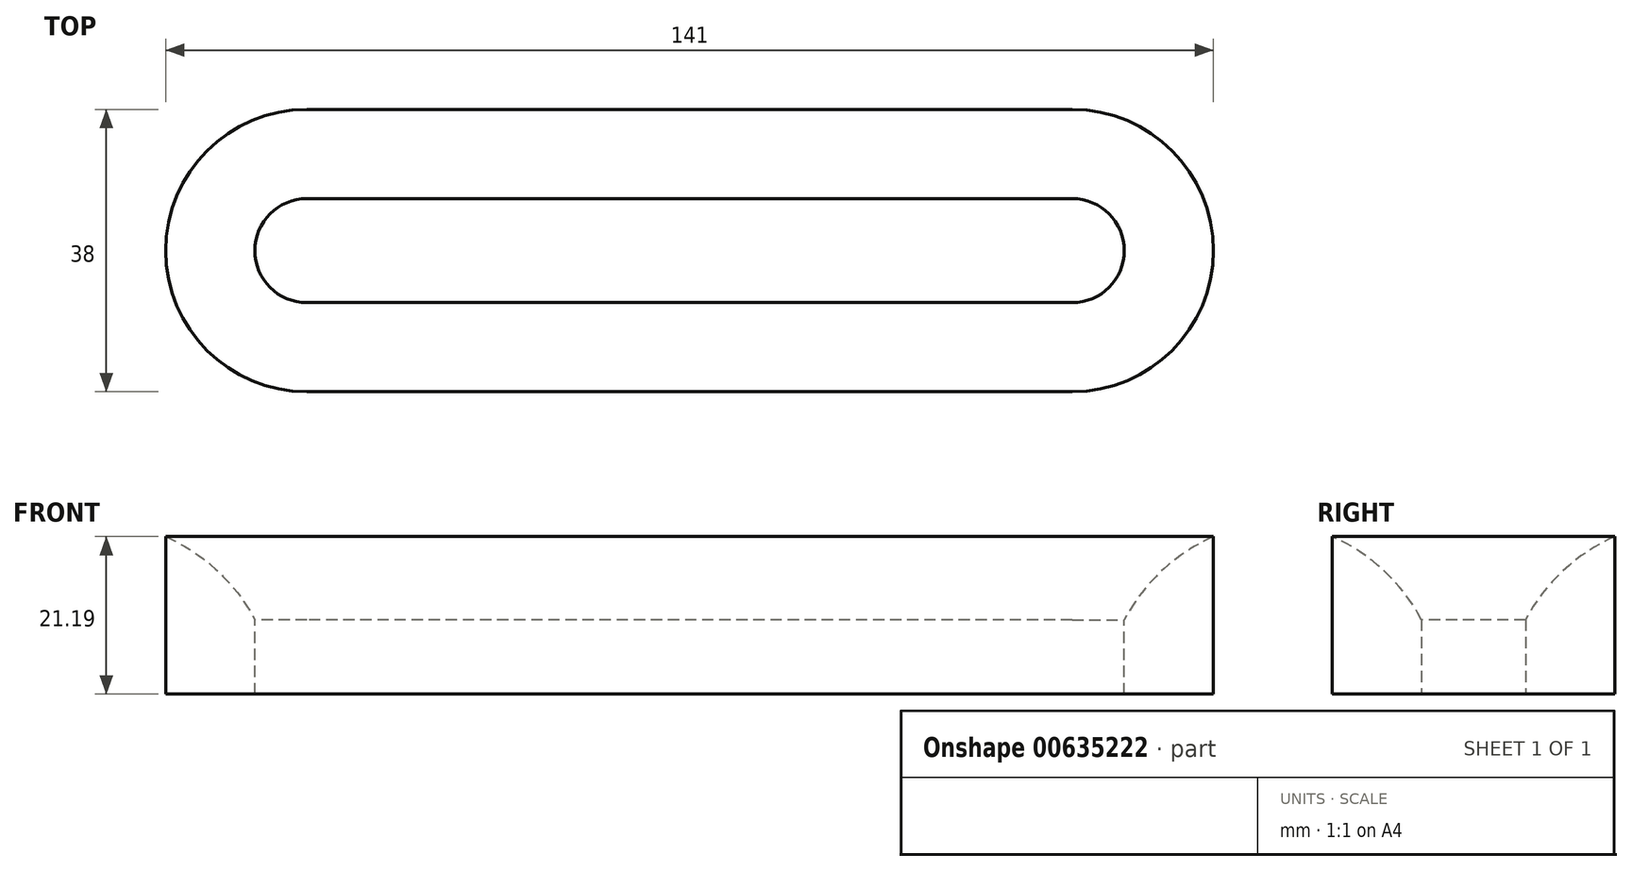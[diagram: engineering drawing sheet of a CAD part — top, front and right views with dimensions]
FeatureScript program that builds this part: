
annotation { "Feature Type Name" : "Feature", "Feature Type Description" : "" }
export const myFeature = defineFeature(function(context is Context, id is Id, definition is map)
    precondition{}
    {
        {
            var Q0;
            Q0=qCreatedBy(makeId("Top.planeOp"),FACE);
            var sketch = newSketch(context, id + "F0", { "sketchPlane" : qUnion([Q0])});
            skLineSegment(sketch, "E0", {"start": v(-51.5, 19) * mm, "end": v(51.5, 19) * mm});
            skLineSegment(sketch, "E1", {"start": v(-51.5, -19) * mm, "end": v(51.5, -19) * mm});
            skArc(sketch, "E2", {"start": v(-51.5, 19) * mm, "mid": v(-70.5, 0) * mm, "end": v(-51.5, -19) * mm});
            skArc(sketch, "E3", {"start": v(51.5, -19) * mm, "mid": v(70.5, 0) * mm, "end": v(51.5, 19) * mm});
            skSolve(sketch);
        }
        {
            var Q0;
            Q0=qCreatedBy(makeId("Right.planeOp"),FACE);
            var sketch = newSketch(context, id + "F1", { "sketchPlane" : qUnion([Q0])});
            skArc(sketch, "E4", {"start": v(-7, -11.2) * mm, "mid": v(-12.06, -4.58) * mm, "end": v(-19, 0) * mm});
            skLineSegment(sketch, "E5", {"start": v(-19, 0) * mm, "end": v(-19, -11.2) * mm});
            skLineSegment(sketch, "E6", {"start": v(-7, -11.2) * mm, "end": v(-7, -21.2) * mm});
            skLineSegment(sketch, "E7", {"start": v(-7, -21.2) * mm, "end": v(-19, -21.2) * mm});
            skLineSegment(sketch, "E8", {"start": v(-19, -21.2) * mm, "end": v(-19, -11.2) * mm});
            skSolve(sketch);
        }
        {
            var Q0;
            Q0=makeQuery(id+"F1.imprint","IMPRINT",FACE,{"disambiguationData":[TD([[makeQuery(id+"F1.imprint","IMPRINT",EDGE,{"derivedFrom":sQuery(id+"F1.wireOp",EDGE,"E4")}),1.0]])]});
            var Q1;
            Q1=sQuery(id+"F0.wireOp",EDGE,"E1");
            var Q2;
            Q2=sQuery(id+"F0.wireOp",EDGE,"E2");
            var Q3;
            Q3=sQuery(id+"F0.wireOp",EDGE,"E0");
            var Q4;
            Q4=sQuery(id+"F0.wireOp",EDGE,"E3");
            sweep(context, id + "F2", {"profiles" : qUnion([Q0]), "path" : qUnion([Q1, Q2, Q3, Q4])});
        }
    });
